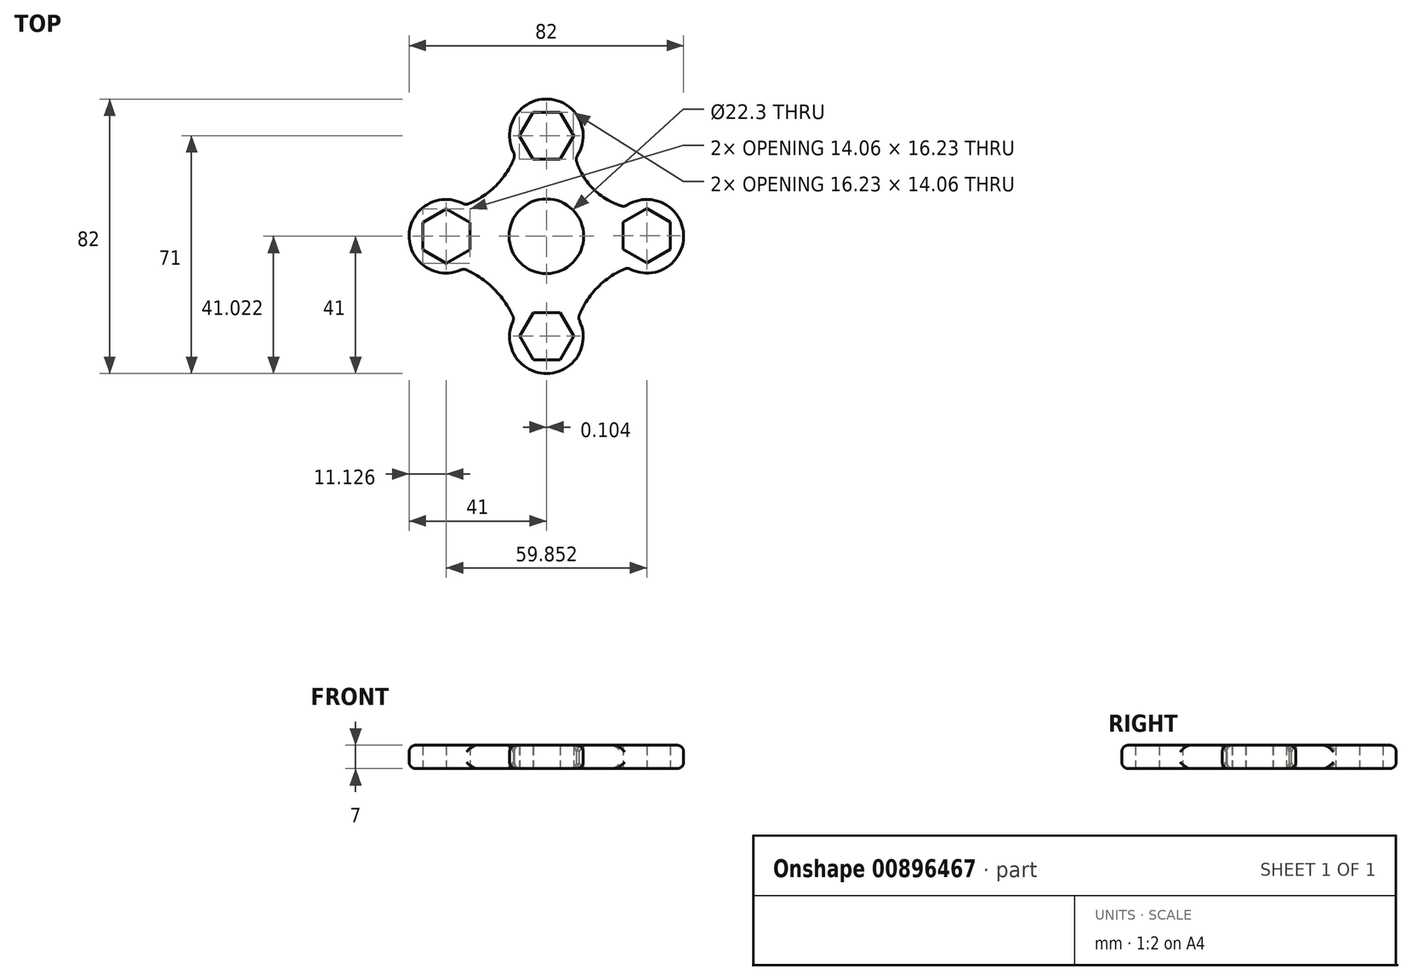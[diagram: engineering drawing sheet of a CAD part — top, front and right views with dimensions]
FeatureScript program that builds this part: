
annotation { "Feature Type Name" : "Feature", "Feature Type Description" : "" }
export const myFeature = defineFeature(function(context is Context, id is Id, definition is map)
    precondition{}
    {
        {
            var Q0;
            Q0=qCreatedBy(makeId("Top.planeOp"),FACE);
            var sketch = newSketch(context, id + "F0", { "sketchPlane" : qUnion([Q0])});
            skCircle(sketch, "E0", {"center": v(0, 0) * mm, "radius": 11.15 * mm});
            skLineSegment(sketch, "E1", {"start": v(0, 0) * mm, "end": v(0, 30) * mm, "construction": true});
            skCircle(sketch, "E2.cCircle", {"center": v(0, 30) * mm, "radius": 7.03 * mm, "construction": true});
            skLineSegment(sketch, "E2.0", {"start": v(4.06, 22.97) * mm, "end": v(-4.06, 22.97) * mm});
            skLineSegment(sketch, "E2.1", {"start": v(-4.06, 22.97) * mm, "end": v(-8.12, 30) * mm});
            skLineSegment(sketch, "E2.2", {"start": v(-8.12, 30) * mm, "end": v(-4.06, 37.03) * mm});
            skLineSegment(sketch, "E2.3", {"start": v(-4.06, 37.03) * mm, "end": v(4.06, 37.03) * mm});
            skLineSegment(sketch, "E2.4", {"start": v(4.06, 37.03) * mm, "end": v(8.12, 30) * mm});
            skLineSegment(sketch, "E2.5", {"start": v(8.12, 30) * mm, "end": v(4.06, 22.97) * mm});
            skPoint(sketch, "E2.0.midPoint", {"position": v(0, 22.97) * mm});
            skLineSegment(sketch, "E3.1.0", {"start": v(0, 0) * mm, "end": v(-25.98, -15) * mm, "construction": true});
            skLineSegment(sketch, "E3.2.0", {"start": v(0, 0) * mm, "end": v(25.98, -15) * mm, "construction": true});
            skCircle(sketch, "E4.1.0", {"center": v(-29.87, 0.02) * mm, "radius": 7.03 * mm, "construction": true});
            skLineSegment(sketch, "E4.1.1", {"start": v(-29.87, 8.14) * mm, "end": v(-22.85, 4.08) * mm});
            skPoint(sketch, "E4.1.2", {"position": v(-22.85, 0.02) * mm});
            skLineSegment(sketch, "E4.1.3", {"start": v(-22.85, -4.04) * mm, "end": v(-29.87, -8.1) * mm});
            skLineSegment(sketch, "E4.1.4", {"start": v(-36.9, -4.04) * mm, "end": v(-36.9, 4.08) * mm});
            skLineSegment(sketch, "E4.1.5", {"start": v(-22.85, 4.08) * mm, "end": v(-22.85, -4.04) * mm});
            skLineSegment(sketch, "E4.1.6", {"start": v(-36.9, 4.08) * mm, "end": v(-29.87, 8.14) * mm});
            skLineSegment(sketch, "E4.1.7", {"start": v(-29.87, -8.1) * mm, "end": v(-36.9, -4.04) * mm});
            skCircle(sketch, "E4.2.0", {"center": v(0.1, -29.85) * mm, "radius": 7.03 * mm, "construction": true});
            skLineSegment(sketch, "E4.2.1", {"start": v(-8.01, -29.85) * mm, "end": v(-3.95, -22.82) * mm});
            skPoint(sketch, "E4.2.2", {"position": v(0.1, -22.82) * mm});
            skLineSegment(sketch, "E4.2.3", {"start": v(4.16, -22.82) * mm, "end": v(8.22, -29.85) * mm});
            skLineSegment(sketch, "E4.2.4", {"start": v(4.16, -36.88) * mm, "end": v(-3.95, -36.88) * mm});
            skLineSegment(sketch, "E4.2.5", {"start": v(-3.95, -22.82) * mm, "end": v(4.16, -22.82) * mm});
            skLineSegment(sketch, "E4.2.6", {"start": v(-3.95, -36.88) * mm, "end": v(-8.01, -29.85) * mm});
            skLineSegment(sketch, "E4.2.7", {"start": v(8.22, -29.85) * mm, "end": v(4.16, -36.88) * mm});
            skPoint(sketch, "E4.center", {"position": v(0.05, 0.07) * mm});
            skLineSegment(sketch, "E5.2.3.0", {"start": v(29.98, -7.99) * mm, "end": v(22.95, -3.93) * mm});
            skPoint(sketch, "E5.5.3.0", {"position": v(22.95, 0.13) * mm});
            skLineSegment(sketch, "E5.6.3.0", {"start": v(22.95, 4.18) * mm, "end": v(29.98, 8.24) * mm});
            skCircle(sketch, "E5.7.3.0", {"center": v(29.98, 0.13) * mm, "radius": 7.03 * mm, "construction": true});
            skLineSegment(sketch, "E5.9.3.0", {"start": v(37, 4.18) * mm, "end": v(37, -3.93) * mm});
            skLineSegment(sketch, "E5.12.3.0", {"start": v(22.95, -3.93) * mm, "end": v(22.95, 4.18) * mm});
            skLineSegment(sketch, "E5.15.3.0", {"start": v(37, -3.93) * mm, "end": v(29.98, -7.99) * mm});
            skLineSegment(sketch, "E5.18.3.0", {"start": v(29.98, 8.24) * mm, "end": v(37, 4.18) * mm});
            skArc(sketch, "E6", {"start": v(8.73, 23.3) * mm, "mid": v(0.54, 40.99) * mm, "end": v(-9.35, 24.2) * mm});
            skArc(sketch, "E7.1.0", {"start": v(-24.21, 9.35) * mm, "mid": v(-41, 0.31) * mm, "end": v(-24.75, -9.67) * mm});
            skArc(sketch, "E7.2.0", {"start": v(-9.63, -24.68) * mm, "mid": v(0.13, -41) * mm, "end": v(9.5, -24.45) * mm});
            skArc(sketch, "E7.3.0", {"start": v(24.3, -9.4) * mm, "mid": v(40.99, 0.54) * mm, "end": v(23.4, 8.8) * mm});
            skArc(sketch, "E8", {"start": v(-24.21, 9.35) * mm, "mid": v(-15.07, 15.07) * mm, "end": v(-9.35, 24.2) * mm});
            skArc(sketch, "E9", {"start": v(8.73, 23.3) * mm, "mid": v(14.08, 14.05) * mm, "end": v(23.4, 8.8) * mm});
            skArc(sketch, "E10", {"start": v(24.3, -9.4) * mm, "mid": v(15.24, -15.3) * mm, "end": v(9.5, -24.45) * mm});
            skArc(sketch, "E11", {"start": v(-9.63, -24.68) * mm, "mid": v(-15.71, -15.69) * mm, "end": v(-24.75, -9.67) * mm});
            skSolve(sketch);
        }
        {
            var Q0;
            Q0 = qSketchRegion(id + "F0", true);
            extrude(context, id + "F1", {"entities" : qUnion([Q0]), "depth" : 7 * mm, "offsetDistance" : 25 * mm});
        }
        {
            var Q0;
            Q0=makeQuery(id+"F1.opExtrude","SWEPT_FACE",FACE,{"disambiguationData":[OSD([sQuery(id+"F0.wireOp",EDGE,"E7.1.0")])]});
            var Q1;
            Q1=makeQuery(id+"F1.opExtrude","SWEPT_FACE",FACE,{"disambiguationData":[OSD([sQuery(id+"F0.wireOp",EDGE,"E7.2.0")])]});
            var Q2;
            Q2=makeQuery(id+"F1.opExtrude","SWEPT_FACE",FACE,{"disambiguationData":[OSD([sQuery(id+"F0.wireOp",EDGE,"E7.3.0")])]});
            var Q3;
            Q3=makeQuery(id+"F1.opExtrude","SWEPT_FACE",FACE,{"disambiguationData":[OSD([sQuery(id+"F0.wireOp",EDGE,"E6")])]});
            fillet(context, id + "F2", {"entities" : qUnion([Q0, Q1, Q2, Q3]), "radius" : 2 * mm, "tangentPropagation" : true, "allowEdgeOverflow" : false});
        }
    });
